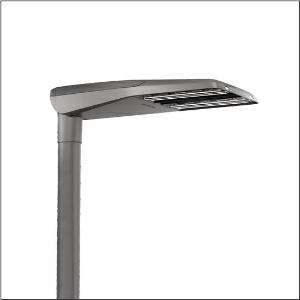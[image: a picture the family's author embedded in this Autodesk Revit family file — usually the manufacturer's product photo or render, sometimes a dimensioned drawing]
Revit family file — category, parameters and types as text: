
# Revit family: streetlight_sl_11_iq_midi___pc-r_5xc3f21f08me_be3f
name_source: partatom
category: Lighting Fixtures
units: mm (PartAtom-declared; Revit-internal decimal feet)

## family parameters
Cut with Voids When Loaded = No
Host = Face
Light Source = No
Part Type = Normal
Room Calculation Point = No
Round Connector Dimension = Use Diameter
Shared = No

## types (1)
- --- (1 x LED, 12740 lm, 124.7 W, 2200K)
    Apparent Load = 125 VA
    CIE Flux Codes = 37 73 96 100 100
    Color Rendering = 70
    Color Temperature = 2200K
    Default Elevation = 1800 mm
    Description = Streetlight SL 11 iQ midi, mast luminaire, primary light control with 3 zone facetted reflector, of plastic, silver coated, highly specular, primary optical cover: cover, of PMMA, transparent, light distribution: PC-R, light emission: direct distribution, primary light characteristic: asymmetric, right, installation type: post-top, side-entry, LED, High Power LED, rated luminous flux: 12.740lm, luminous efficacy: 102lm/W, light colour: 722, colour temperature: 2200K, control: Street-Remote, optimised constant luminous flux control (CLO 2.0), Desk-Remote (wireless, voltage-free reading and setting of iQ features in the workshop via application-optimized NFC function/RFID function), Light-Fading, Smart-Wire, Night-Set, Lumen-Switch, Temp-Guard, Auto-Match, with cable H07RN-F 5x 1.5mm², mains connection: 230..240V, AC, 50/60Hz, connection cable pre-assembled, cable length: 12,5m, start of lifetime: 125W, end of service life: 132W, reduction: 57W, luminaire housing, of diecast aluminium, powder-coated, Siteco® metallic grey (DB 702S), please order mast flange separately, inclination adjustable without tools: 0°, 5°, 10°, 15° (post-top) | 0°, -5°, -10°, -15° (side-entry), sealing non-destructively replaceable, multi-level sealing system, length: 780mm, width: 376mm, height: 118mm, mast flange for spigot size: 42mm (side-entry): 5XC10008XM4, 60/48mm (side-entry/post-top): 5XC10108XM2, 76/60mm (side-entry/post-top): 5XC10108XM1, equipment: Power, protection rating (complete): IP66, insulation class (complete): insulation class II (safety insulation), certification: CE, ENEC, VDE, impact resistance: IK09, permissible operating ambient temperature for outdoor applications: -25..+50°C, standard-compliant lighting for roads and squares, Environmental Product Declaration (EPD) tested and certified by an independent institute, packaging unit: 1 piece

Light Distribution: PC-R
    Height = 118 mm
    Lamp = 1 x LED
    Lamp Light Flux = 12740 lm
    Lamp Power = 124.7 W
    Lamp count = 1
    Length = 780 mm
    Luminous efficacy = 102 lm/W
    Manufacturer = Siteco
    ModVariant = No
    Model = 5XC3F21F08ME
    Number of Poles = 1
    OnlyDefault = Yes
    Power Factor = 1
    Product Name = Streetlight SL 11 iQ midi | PC-R
    Product group = mast luminaire | pylon top
    ProductGroupID = 6100
    Protection Class = Protection class II
    Protection Degree = IP 66
    RLX_Detail_Level = 1
    RLX_Emergency_Light_Flux = 0 lm
    RLX_Emergency_Type = 0
    RLX_Emergency_Type_DB = No
    RlxData = <blob elided: 74289 chars, md5=56d1bfa8>
    Socket = socket
    Standby Power = 0 W
    System Light Flux = 12741 lm
    System Power = 125 W
    Type Comments = factory setting: luminous flux: 100 % | dim-lin: 254 | 557 mA
    Type Image = l_1005960.jpg
    URL = http://relux.com
    VarID = @adj_076305
    Voltage = 0 V
    Weight = 0.00 kg
    Width = 376 mm

## geometry (parser evidence)
native form markers: Blend x4, Sweep x10
no freeform markers — native parametric forms only
